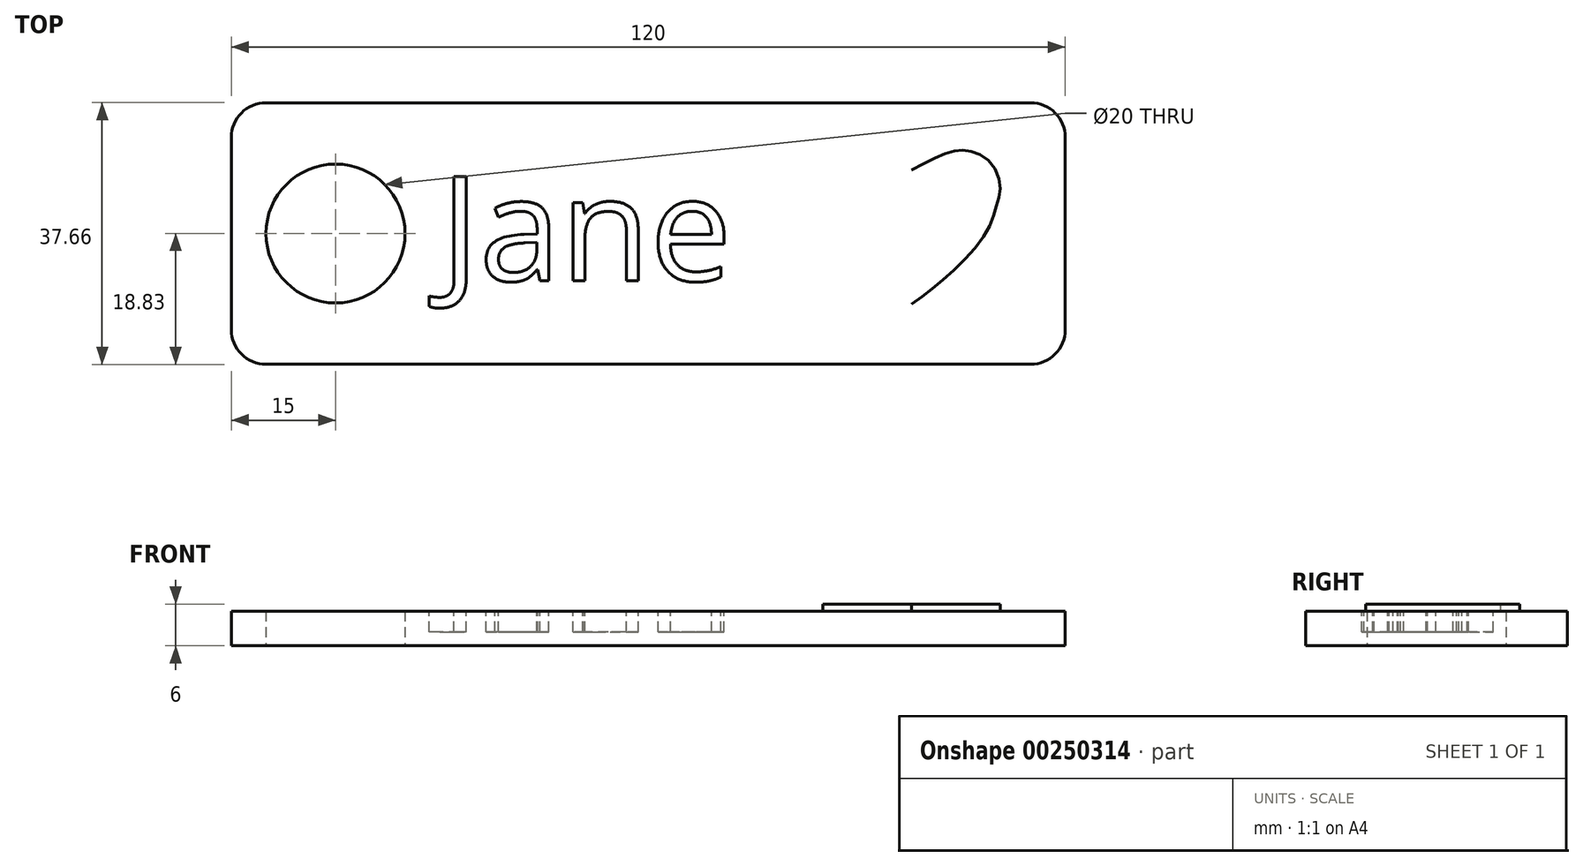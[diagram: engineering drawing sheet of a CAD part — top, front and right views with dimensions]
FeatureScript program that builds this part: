
annotation { "Feature Type Name" : "Feature", "Feature Type Description" : "" }
export const myFeature = defineFeature(function(context is Context, id is Id, definition is map)
    precondition{}
    {
        {
            var Q0;
            Q0=qCreatedBy(makeId("Top.planeOp"),FACE);
            var sketch = newSketch(context, id + "F0", { "sketchPlane" : qUnion([Q0])});
            skLineSegment(sketch, "E0.bottom", {"start": v(-60, 18.83) * mm, "end": v(60, 18.83) * mm});
            skLineSegment(sketch, "E0.top", {"start": v(-60, -18.83) * mm, "end": v(60, -18.83) * mm});
            skLineSegment(sketch, "E0.left", {"start": v(-60, 18.83) * mm, "end": v(-60, -18.83) * mm});
            skLineSegment(sketch, "E0.right", {"start": v(60, 18.83) * mm, "end": v(60, -18.83) * mm});
            skPoint(sketch, "E0.middle", {"position": v(0, 0) * mm});
            skCircle(sketch, "E1", {"center": v(-45, 0) * mm, "radius": 10 * mm});
            skSolve(sketch);
        }
        {
            var Q0;
            Q0 = qSketchRegion(id + "F0", true);
            extrude(context, id + "F1", {"entities" : qUnion([Q0]), "depth" : 5 * mm});
        }
        {
            var Q0;
            Q0=makeQuery(id+"F1.opExtrude","SWEPT_EDGE",EDGE,{"disambiguationData":[OSD([sQuery(id+"F0.wireOp",EDGE,"E0.bottom"),sQuery(id+"F0.wireOp",EDGE,"E0.right")])]});
            var Q1;
            Q1=makeQuery(id+"F1.opExtrude","SWEPT_EDGE",EDGE,{"disambiguationData":[OSD([sQuery(id+"F0.wireOp",EDGE,"E0.bottom"),sQuery(id+"F0.wireOp",EDGE,"E0.left")])]});
            var Q2;
            Q2=makeQuery(id+"F1.opExtrude","SWEPT_EDGE",EDGE,{"disambiguationData":[OSD([sQuery(id+"F0.wireOp",EDGE,"E0.top"),sQuery(id+"F0.wireOp",EDGE,"E0.left")])]});
            var Q3;
            Q3=makeQuery(id+"F1.opExtrude","SWEPT_EDGE",EDGE,{"disambiguationData":[OSD([sQuery(id+"F0.wireOp",EDGE,"E0.top"),sQuery(id+"F0.wireOp",EDGE,"E0.right")])]});
            fillet(context, id + "F2", {"entities" : qUnion([Q0, Q1, Q2, Q3]), "radius" : 5 * mm, "tangentPropagation" : true, "allowEdgeOverflow" : false});
        }
        {
            var Q0;
            Q0=makeQuery(id+"F1.opExtrude","CAP_FACE",FACE,{"disambiguationData":[OSD([sQuery(id+"F0.wireOp",EDGE,"E0.bottom"),sQuery(id+"F0.wireOp",EDGE,"E0.top"),sQuery(id+"F0.wireOp",EDGE,"E0.left"),sQuery(id+"F0.wireOp",EDGE,"E0.right"),sQuery(id+"F0.wireOp",EDGE,"E1")])],"isStart":false});
            var sketch = newSketch(context, id + "F3", { "sketchPlane" : qUnion([Q0])});
            skText(sketch, "E2", { "text": "Jane", "fontName": "OpenSans-Regular.ttf"});
            const initialGuessF3  = {"E2": [-0.0299, -0.0068, 1, 0, 0.0151]};
            skSetInitialGuess(sketch, initialGuessF3);
            skSolve(sketch);
        }
        {
            var Q0;
            Q0 = qSketchRegion(id + "F3", true);
            extrude(context, id + "F4", {"entities" : qUnion([Q0]), "operationType" : NewBodyOperationType.REMOVE, "oppositeDirection" : true, "depth" : 3 * mm});
        }
        {
            var Q0;
            {var subQ0=sQuery(id+"F0.wireOp",EDGE,"E0.top");var subQ1=sQuery(id+"F0.wireOp",EDGE,"E0.left");var subQ2=sQuery(id+"F0.wireOp",EDGE,"E0.bottom");var subQ3=sQuery(id+"F0.wireOp",EDGE,"E1");var subQ4=sQuery(id+"F0.wireOp",EDGE,"E0.right");Q0=makeQuery(id+"F4.boolean.opBoolean","SPLIT",FACE,{"disambiguationData":[TD([makeQuery(id+"F1.opExtrude","SWEPT_FACE",FACE,{"disambiguationData":[OSD([subQ2])]})])],"derivedFrom":makeQuery(id+"F1.opExtrude","CAP_FACE",FACE,{"disambiguationData":[OSD([subQ2,subQ0,subQ1,subQ4,subQ3])],"isStart":false})});}
            var sketch = newSketch(context, id + "F5", { "sketchPlane" : qUnion([Q0])});
            skSolve(sketch);
        }
        {
            var Q0;
            Q0=qCreatedBy(makeId("Top.planeOp"),FACE);
            var sketch = newSketch(context, id + "F6", { "sketchPlane" : qUnion([Q0])});
            skLineSegment(sketch, "E3", {"start": v(37.9, 31.97) * mm, "end": v(37.9, -39.37) * mm, "construction": true});
            skFitSpline(sketch, "E4", {"points": [v(37.9, 9.16) * mm, v(32.82, 11.6) * mm, v(30.03, 11.94) * mm, v(27.07, 10.72) * mm, v(25.16, 7.07) * mm, v(25.68, 4.1) * mm, v(27.25, 0) * mm, v(32.65, -6) * mm, v(37.9, -10.18) * mm], "startDerivative": vector(-39.28, 21.14) * mm, "endDerivative": vector(33.77, -25.37) * mm});
            skFitSpline(sketch, "E5.MirrorCS", {"points": [v(37.9, 9.16) * mm, v(42.97, 11.6) * mm, v(45.76, 11.94) * mm, v(48.72, 10.72) * mm, v(50.63, 7.07) * mm, v(50.11, 4.1) * mm, v(48.54, 0) * mm, v(43.14, -6) * mm, v(37.9, -10.18) * mm], "startDerivative": vector(39.28, 21.14) * mm, "endDerivative": vector(-33.77, -25.37) * mm});
            skSolve(sketch);
        }
        {
            var Q0;
            Q0 = qSketchRegion(id + "F6", true);
            extrude(context, id + "F7", {"entities" : qUnion([Q0]), "operationType" : NewBodyOperationType.ADD, "depth" : 6 * mm});
        }
    });
